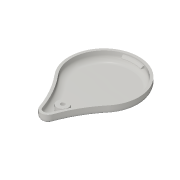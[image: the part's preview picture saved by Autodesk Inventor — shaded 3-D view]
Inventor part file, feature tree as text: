
AUTODESK INVENTOR PART (.ipt)
format: ipt  version: 2016 SP1 (Build 200210100, 210)  size: 235,008 bytes
history: native  units: mm
features: extrude x6, sketch x6, projected_geometry x4, plane x1, chamfer x1, fillet x1
ambient origin geometry x8: Origin, YZ Plane, XZ Plane, XY Plane, X Axis, Y Axis, Z Axis, Center Point
bodies: Volumenkörper1 (feature_tree)
feature tree (19):
  extrude  "Extrusion1"  Depth=32.9mm
  extrude  "Extrusion13"  Depth=6.6mm
  extrude  "Extrusion14"  Depth=55.0mm
  extrude  "Extrusion15"  Depth=4.1mm TaperAngle=0.0deg
  extrude  "Extrusion16"  Depth=1.2mm
  plane  "Arbeitsebene1"
  extrude  "Extrusion17"  Depth=55.0mm
  chamfer  "Fase1"  Distance=4.0mm
  fillet  "Rundung6"  Radius=5.5mm
  sketch  "Skizze1"  dims[d0=30.7mm d1=32.9mm]
  sketch  "Skizze13"  dims[d2=46.0mm d3=6.6mm]
  projected_geometry  "Projizierte Kontur11"
  sketch  "Skizze14"  dims[d4=55.0mm d5=55.0mm]
  projected_geometry  "Projizierte Kontur12"
  sketch  "Skizze15"  dims[d6=0.992569mm d7=4.1mm d8=0.0mm]
  projected_geometry  "Projizierte Kontur13"
  sketch  "Skizze16"  dims[d92=1.2mm d93=1.2mm]
  sketch  "Skizze17"  dims[d94=55.0mm d95=55.0mm d96=4.0mm d97=0.0mm d98=5.5mm d99=9.0mm d100=2.6mm d101=0.0mm d102=4.0mm d103=2.5mm d104=0.0mm d105=1.9mm d106=2.6mm d107=0.0mm d108=-0.6mm d109=9.6mm d110=1.4mm d111=1.4mm d112=1.4mm d113=1.0mm d114=0.0mm d115=0.8mm d116=2.0mm d117=45.0deg d119=2.5mm]
  projected_geometry  "Projizierte Kontur14"
